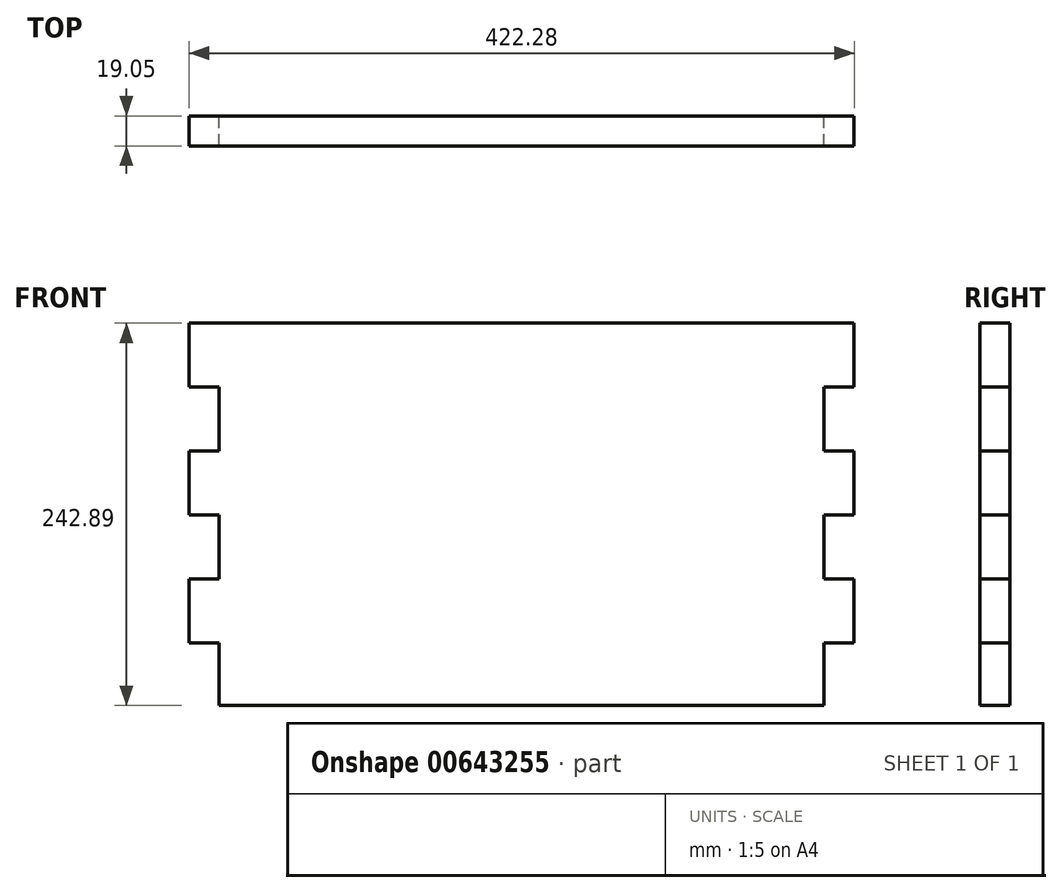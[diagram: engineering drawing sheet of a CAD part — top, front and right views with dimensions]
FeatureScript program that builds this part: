
annotation { "Feature Type Name" : "Feature", "Feature Type Description" : "" }
export const myFeature = defineFeature(function(context is Context, id is Id, definition is map)
    precondition{}
    {
        {
            var Q0;
            Q0=qCreatedBy(makeId("Front.planeOp"),FACE);
            var sketch = newSketch(context, id + "F0", { "sketchPlane" : qUnion([Q0])});
            skLineSegment(sketch, "E0.top", {"start": v(-193.16, 63.84) * mm, "end": v(-174.1, 63.84) * mm});
            skLineSegment(sketch, "E0.left", {"start": v(-193.16, 104.48) * mm, "end": v(-193.16, 63.84) * mm});
            skLineSegment(sketch, "E1.0.1.0", {"start": v(-193.16, 23.2) * mm, "end": v(-174.1, 23.2) * mm});
            skLineSegment(sketch, "E1.0.1.1", {"start": v(-174.1, 63.84) * mm, "end": v(-174.1, 23.2) * mm});
            skLineSegment(sketch, "E1.0.2.0", {"start": v(-193.16, -17.44) * mm, "end": v(-174.1, -17.44) * mm});
            skLineSegment(sketch, "E1.0.2.2", {"start": v(-193.16, 23.2) * mm, "end": v(-193.16, -17.44) * mm});
            skLineSegment(sketch, "E1.0.2.3", {"start": v(-193.16, 23.2) * mm, "end": v(-174.1, 23.2) * mm});
            skLineSegment(sketch, "E1.0.3.0", {"start": v(-193.16, -58.08) * mm, "end": v(-174.1, -58.08) * mm});
            skLineSegment(sketch, "E1.0.3.1", {"start": v(-174.1, -17.44) * mm, "end": v(-174.1, -58.08) * mm});
            skLineSegment(sketch, "E1.0.3.3", {"start": v(-193.16, -17.44) * mm, "end": v(-174.1, -17.44) * mm});
            skLineSegment(sketch, "E1.0.4.0", {"start": v(-193.16, -98.72) * mm, "end": v(-174.1, -98.72) * mm});
            skLineSegment(sketch, "E1.0.4.2", {"start": v(-193.16, -58.08) * mm, "end": v(-193.16, -98.72) * mm});
            skLineSegment(sketch, "E1.0.4.3", {"start": v(-193.16, -58.08) * mm, "end": v(-174.1, -58.08) * mm});
            skLineSegment(sketch, "E1.0.5.3", {"start": v(-193.16, -98.72) * mm, "end": v(-174.1, -98.72) * mm});
            skLineSegment(sketch, "E2", {"start": v(-174.1, -98.72) * mm, "end": v(-174.1, -138.4) * mm});
            skLineSegment(sketch, "E3", {"start": v(-193.16, 104.48) * mm, "end": v(17.98, 104.48) * mm});
            skLineSegment(sketch, "E4", {"start": v(-174.1, -138.4) * mm, "end": v(17.98, -138.4) * mm});
            skLineSegment(sketch, "E5.MirrorCS", {"start": v(229.12, 63.84) * mm, "end": v(210.07, 63.84) * mm});
            skLineSegment(sketch, "E6.MirrorCS", {"start": v(229.12, -58.08) * mm, "end": v(210.07, -58.08) * mm});
            skLineSegment(sketch, "E7.MirrorCS", {"start": v(229.12, 23.2) * mm, "end": v(210.07, 23.2) * mm});
            skLineSegment(sketch, "E8.MirrorCS", {"start": v(229.12, -98.72) * mm, "end": v(210.07, -98.72) * mm});
            skLineSegment(sketch, "E9.MirrorCS", {"start": v(229.12, -17.44) * mm, "end": v(210.07, -17.44) * mm});
            skLineSegment(sketch, "E10.MirrorCS", {"start": v(210.07, -98.72) * mm, "end": v(210.07, -138.4) * mm});
            skLineSegment(sketch, "E11.MirrorCS", {"start": v(229.12, -58.08) * mm, "end": v(229.12, -98.72) * mm});
            skLineSegment(sketch, "E12.MirrorCS", {"start": v(229.12, 104.48) * mm, "end": v(229.12, 63.84) * mm});
            skLineSegment(sketch, "E13.MirrorCS", {"start": v(229.12, 23.2) * mm, "end": v(229.12, -17.44) * mm});
            skLineSegment(sketch, "E14.MirrorCS", {"start": v(210.07, -17.44) * mm, "end": v(210.07, -58.08) * mm});
            skLineSegment(sketch, "E15.MirrorCS", {"start": v(210.07, 63.84) * mm, "end": v(210.07, 23.2) * mm});
            skLineSegment(sketch, "E16.MirrorCS", {"start": v(210.07, -138.4) * mm, "end": v(17.98, -138.4) * mm});
            skLineSegment(sketch, "E17.MirrorCS", {"start": v(229.12, 104.48) * mm, "end": v(17.98, 104.48) * mm});
            skSolve(sketch);
        }
        {
            var Q0;
            Q0=qSketchRegion(id+"F0",true);
            extrude(context, id + "F1", {"entities" : qUnion([Q0]), "depth" : 19.05 * mm});
        }
    });
